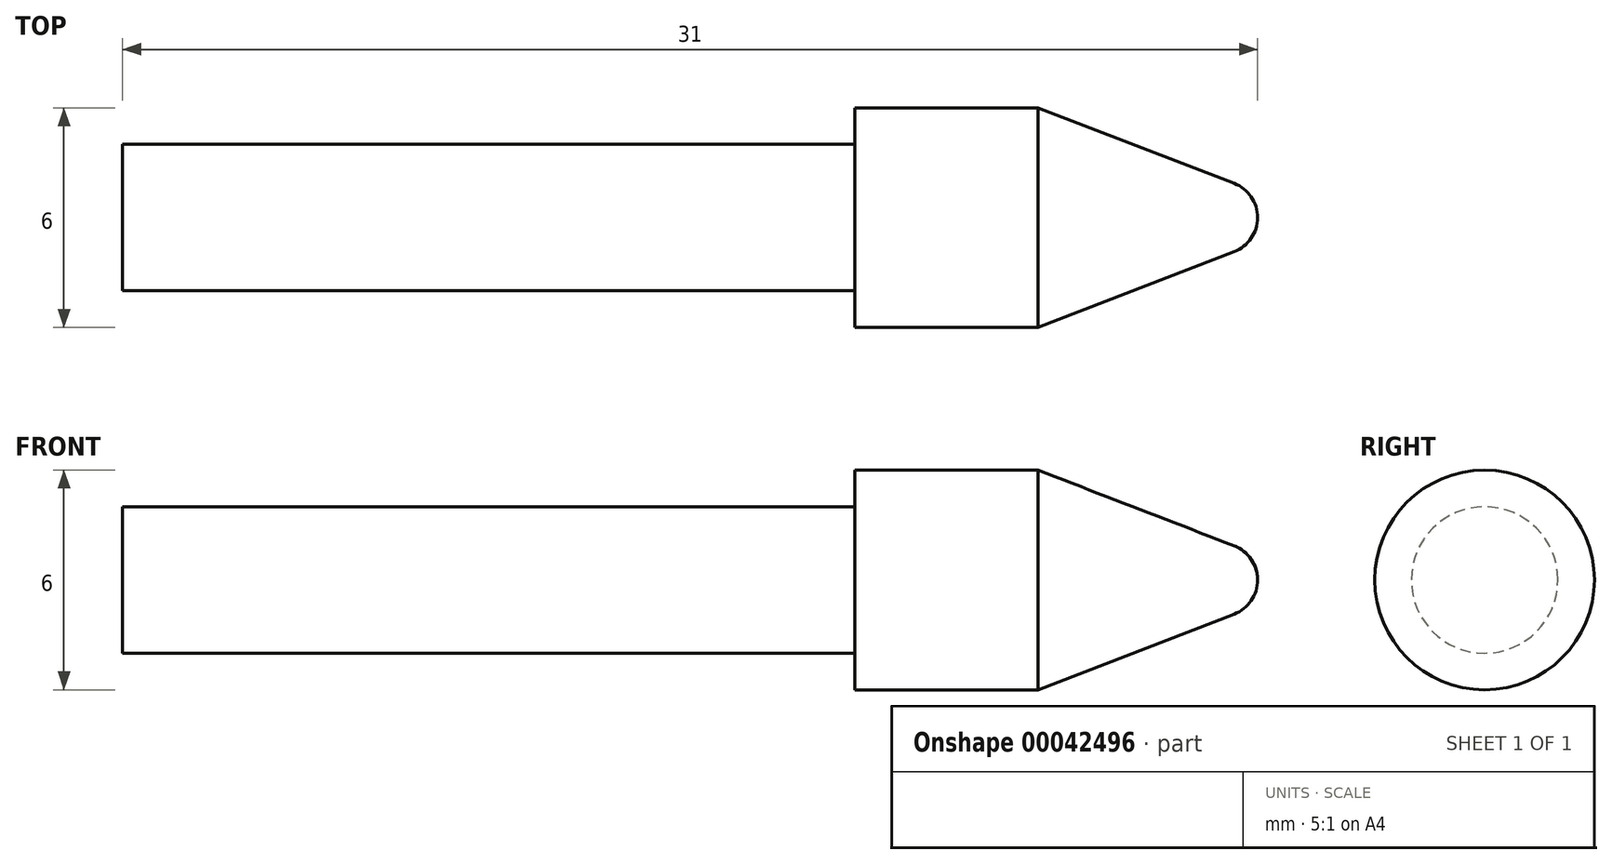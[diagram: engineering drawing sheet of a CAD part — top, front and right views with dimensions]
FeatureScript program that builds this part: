
annotation { "Feature Type Name" : "Feature", "Feature Type Description" : "" }
export const myFeature = defineFeature(function(context is Context, id is Id, definition is map)
    precondition{}
    {
        {
            var Q0;
            Q0=qCreatedBy(makeId("Front.planeOp"),FACE);
            var sketch = newSketch(context, id + "F0", { "sketchPlane" : qUnion([Q0])});
            skLineSegment(sketch, "E0", {"start": v(0, 0) * mm, "end": v(30, 0) * mm});
            skArc(sketch, "E1", {"start": v(31, 0) * mm, "mid": v(30.82, 0.57) * mm, "end": v(30.36, 0.93) * mm});
            skLineSegment(sketch, "E2", {"start": v(0, 0) * mm, "end": v(0, 2) * mm});
            skLineSegment(sketch, "E3", {"start": v(0, 2) * mm, "end": v(20, 2) * mm});
            skLineSegment(sketch, "E4", {"start": v(20, 2) * mm, "end": v(20, 3) * mm});
            skLineSegment(sketch, "E5", {"start": v(20, 3) * mm, "end": v(25, 3) * mm});
            skLineSegment(sketch, "E6", {"start": v(25, 3) * mm, "end": v(30.36, 0.93) * mm});
            skLineSegment(sketch, "E7", {"start": v(30, 0) * mm, "end": v(31, 0) * mm});
            skSolve(sketch);
        }
        {
            var Q0;
            Q0=makeQuery(id+"F0.imprint","IMPRINT",FACE,{"disambiguationData":[TD([[makeQuery(id+"F0.imprint","IMPRINT",EDGE,{"derivedFrom":sQuery(id+"F0.wireOp",EDGE,"E0")}),1.0]])]});
            var Q1;
            Q1=sQuery(id+"F0.wireOp",EDGE,"E0");
            revolve(context, id + "F1", {"entities" : qUnion([Q0]), "axis" : qUnion([Q1]), "revolveType" : RevolveType.FULL});
        }
    });
